# Revit family: Electrical_Equipment-Poke_Through-Hubbell_Wiring-System_One-S1R4
name_source: partatom
category: Electrical Fixtures
revit_build: Autodesk Revit 2015 (Build: 20140606_1530(x64)
units: mm (PartAtom-declared; Revit-internal decimal feet)

## types (1)
- Standard
    Annotation = Yes
    Apparent Load = 2400 VA
    Assembly Code = D5020115
    Conduit Connector 1 Description = Conduit Connector 1
    Conduit Connector 2 Description = Conduit Connector 2
    Conduit Connector 3 Description = Conduit Connector 3
    Conduit Connector 4 Description = Conduit Connector 4
    Conduit Connector 5 Description = Conduit Connector 5
    Default Elevation = 48.00"
    Description = System One - 4 inch Poke Through
    Electrical Connector Description = Power Connector
    Hardware Finish = Metal-Hubbell-Aluminum
    Manufacturer = Hubbell Wiring Device Kellems
    Manufacturer Fax = 203.882.4849
    Model = S1R4PT
    Number of Poles = 1
    Power Factor = 1
    Product Page URL = http://ecatalog.hubbell-wiring.com
    Product data url = https://bimobject.com
    URL = http://www.hubbell-wiring.com
    Voltage = 120 V

## geometry (parser evidence)
native form markers: Blend x10, Sweep x6
no freeform markers — native parametric forms only
